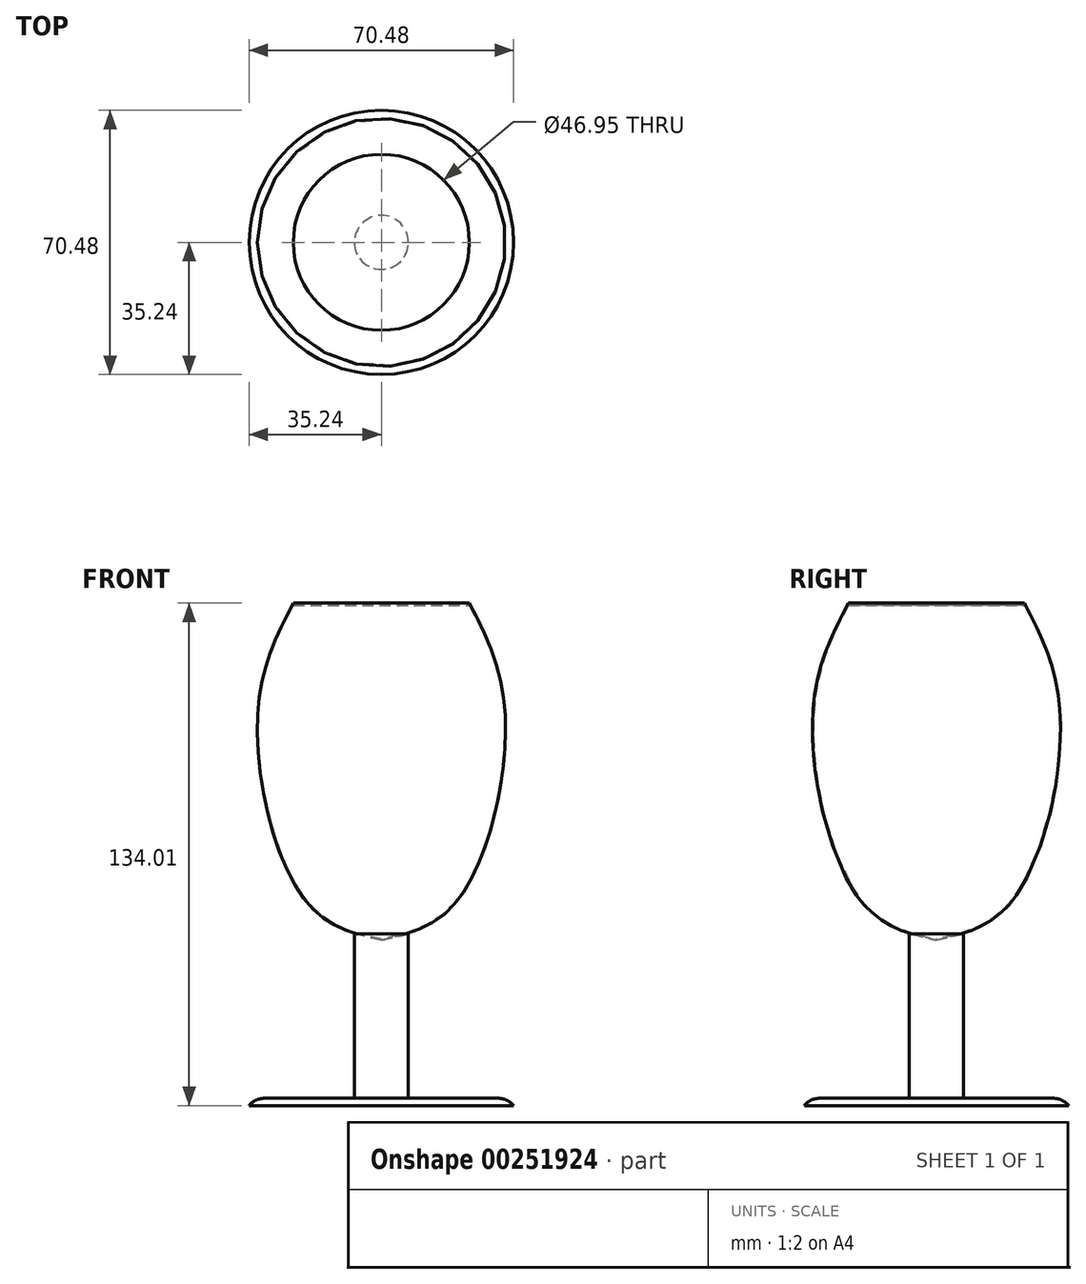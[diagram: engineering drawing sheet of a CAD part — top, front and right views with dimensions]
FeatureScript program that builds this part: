
annotation { "Feature Type Name" : "Feature", "Feature Type Description" : "" }
export const myFeature = defineFeature(function(context is Context, id is Id, definition is map)
    precondition{}
    {
        {
            var Q0;
            Q0=qCreatedBy(makeId("Front.planeOp"),FACE);
            var sketch = newSketch(context, id + "F0", { "sketchPlane" : qUnion([Q0])});
            skLineSegment(sketch, "E0", {"start": v(0, 79.79) * mm, "end": v(0, -78.68) * mm, "construction": true});
            skLineSegment(sketch, "E1", {"start": v(0, -78.68) * mm, "end": v(-35.24, -78.68) * mm});
            skLineSegment(sketch, "E2", {"start": v(0, -78.68) * mm, "end": v(0, -34.56) * mm});
            skFitSpline(sketch, "E3", {"points": [v(0, -34.56) * mm, v(-20.12, -24.2) * mm, v(-33, 25.93) * mm, v(-23.48, 55.33) * mm], "startDerivative": vector(-79.57, 18.1) * mm, "endDerivative": vector(41.54, 79.6) * mm});
            skLineSegment(sketch, "E4", {"start": v(0, 55.33) * mm, "end": v(0, -34.56) * mm, "construction": true});
            skLineSegment(sketch, "E5", {"start": v(0, -78.68) * mm, "end": v(0, 55.33) * mm, "construction": true});
            skFitSpline(sketch, "E6", {"points": [v(-23.48, 55.33) * mm, v(0, 55.33) * mm], "startDerivative": vector(23.48, 0) * mm, "endDerivative": vector(23.48, 0) * mm});
            skLineSegment(sketch, "E7", {"start": v(0, -78.68) * mm, "end": v(0, 55.33) * mm});
            skLineSegment(sketch, "E8", {"start": v(-7.2, -32.92) * mm, "end": v(-7.2, -78.68) * mm});
            skLineSegment(sketch, "E9", {"start": v(-35.24, -78.68) * mm, "end": v(-35.24, -76.75) * mm});
            skLineSegment(sketch, "E10", {"start": v(-35.24, -76.75) * mm, "end": v(-7.2, -76.75) * mm});
            skLineSegment(sketch, "E11", {"start": v(-7.2, -78.68) * mm, "end": v(-7.2, -32.92) * mm});
            skLineSegment(sketch, "E12", {"start": v(0, -34.56) * mm, "end": v(-7.2, -32.92) * mm});
            skSolve(sketch);
        }
        {
            var Q0;
            Q0 = qSketchRegion(id + "F0", true);
            var Q1;
            Q1=sQuery(id+"F0.wireOp",EDGE,"E7");
            revolve(context, id + "F1", {"entities" : qUnion([Q0]), "axis" : qUnion([Q1]), "revolveType" : RevolveType.FULL});
        }
        {
            var Q0;
            Q0=makeQuery(id+"F1.opRevolve","SWEPT_EDGE",EDGE,{"disambiguationData":[OSD([sQuery(id+"F0.wireOp",EDGE,"E9"),sQuery(id+"F0.wireOp",EDGE,"E10")])]});
            fillet(context, id + "F2", {"entities" : qUnion([Q0]), "radius" : 5.08 * mm, "tangentPropagation" : true, "allowEdgeOverflow" : false});
        }
        {
            var Q0;
            Q0=makeQuery(id+"F1.opRevolve","SWEPT_FACE",FACE,{"disambiguationData":[OSD([sQuery(id+"F0.wireOp",EDGE,"E3")])]});
            var Q1;
            Q1=makeQuery(id+"F1.opRevolve","SWEPT_BODY",BODY,{"disambiguationData":[OSD([sQuery(id+"F0.wireOp",EDGE,"E3"),sQuery(id+"F0.wireOp",EDGE,"E6"),sQuery(id+"F0.wireOp",EDGE,"E7")])]});
            shell(context, id + "F3", {"isHollow" : true, "entities" : qUnion([Q0]), "parts" : qUnion([Q1]), "thickness" : 0.25 * mm});
        }
        {
            var Q0;
            Q0=makeQuery(id+"F1.opRevolve","SWEPT_FACE",FACE,{"disambiguationData":[OSD([sQuery(id+"F0.wireOp",EDGE,"E6")])]});
            extrude(context, id + "F4", {"entities" : qUnion([Q0]), "operationType" : NewBodyOperationType.REMOVE, "oppositeDirection" : true, "depth" : 72.9 * mm});
        }
    });
